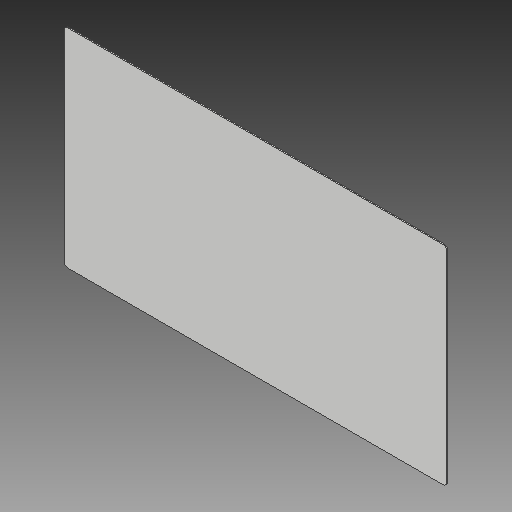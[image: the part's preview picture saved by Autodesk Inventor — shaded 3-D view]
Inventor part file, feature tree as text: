
AUTODESK INVENTOR PART (.ipt)
format: ipt  version: 2019 (Build 230136000, 136)  size: 97,792 bytes
history: native  units: mm
features: other x5, reference x4, extrude x1, sketch x1, helix x1
ambient origin geometry x8: Origin, YZ Plane, XZ Plane, XY Plane, X Axis, Y Axis, Z Axis, Center Point
bodies: Solid1 (feature_tree)
feature tree (12):
  extrude  "Extrusion1"  Depth=3.0mm TaperAngle=0.0deg
  sketch  "Sketch1"  dims[d0=10.0mm d1=3.0mm d2=0.0mm]
  reference  "Reference1"
  reference  "Reference2"
  reference  "Reference3"
  reference  "Reference4"
  other  "<userpath>\Documents\CAD Files\Helix DLP\Helix DLP.iam"
  helix  "Helix DLP.iam"  [1 undecoded]
  other  "30X30 - T-slot - Aluminium Profile_CPY_CPY:1"
  other  "30X30 - T-slot - Aluminium Profile:6"
  other  "30X30 - T-slot - Aluminium Profile:3"
  other  "30X30 - T-slot - Aluminium Profile_CPY_CPY:3"
note: 1 required parameter value undecoded (feature->parameter linkage not recoverable at this tier; creation-order binding heuristic only, values carry confidence <= 0.55)
